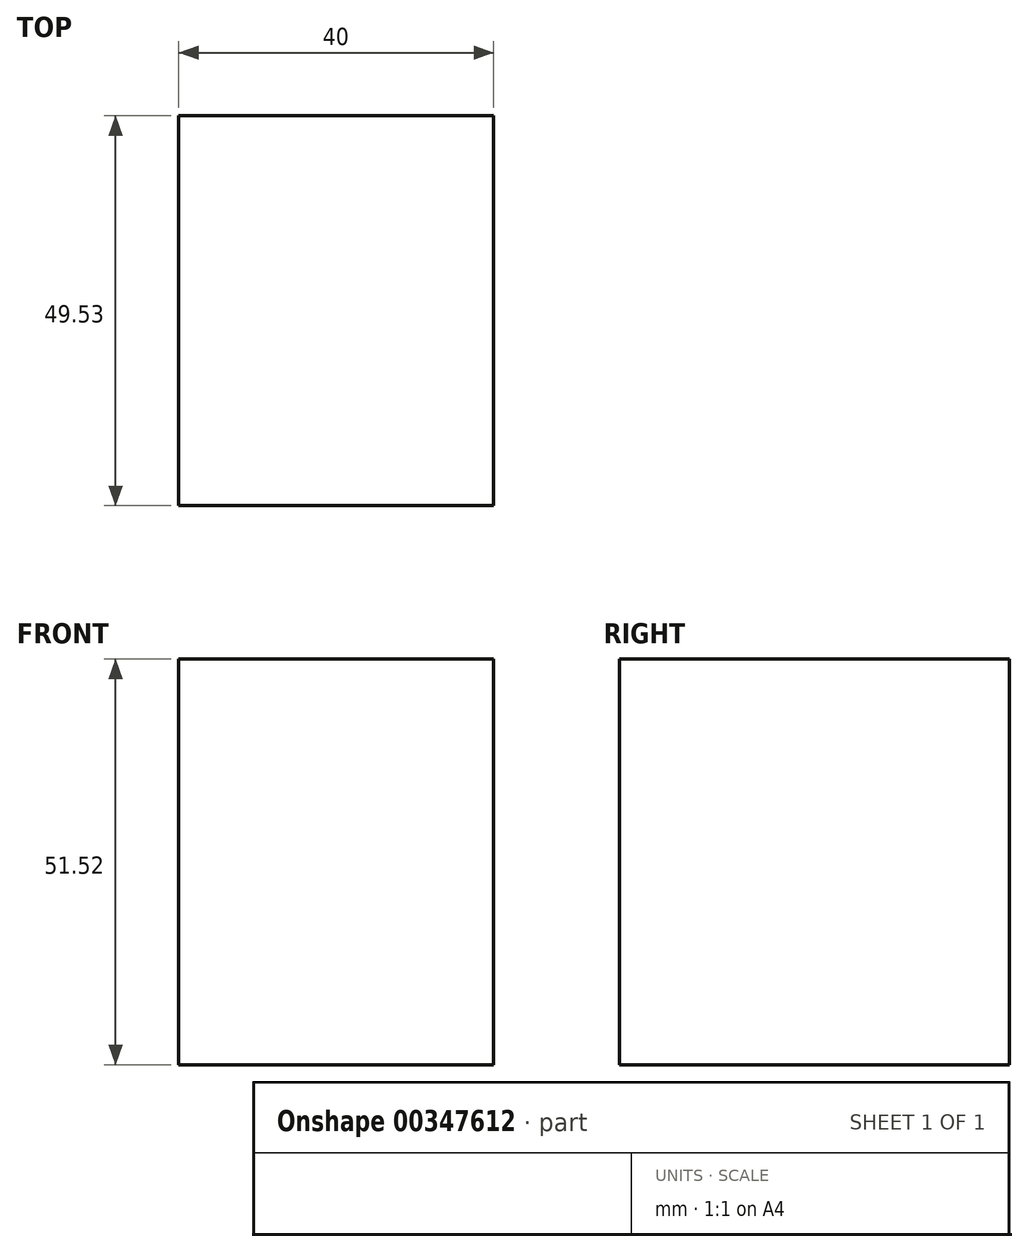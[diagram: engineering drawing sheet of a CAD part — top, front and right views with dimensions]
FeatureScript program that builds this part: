
annotation { "Feature Type Name" : "Feature", "Feature Type Description" : "" }
export const myFeature = defineFeature(function(context is Context, id is Id, definition is map)
    precondition{}
    {
        {
            var Q0;
            Q0=qCreatedBy(makeId("Front.planeOp"),FACE);
            var sketch = newSketch(context, id + "F0", { "sketchPlane" : qUnion([Q0])});
            skLineSegment(sketch, "E0.bottom", {"start": v(-54.68, 26.77) * mm, "end": v(-14.68, 26.77) * mm});
            skLineSegment(sketch, "E0.top", {"start": v(-54.68, -24.75) * mm, "end": v(-14.68, -24.75) * mm});
            skLineSegment(sketch, "E0.left", {"start": v(-54.68, 26.77) * mm, "end": v(-54.68, -24.75) * mm});
            skLineSegment(sketch, "E0.right", {"start": v(-14.68, 26.77) * mm, "end": v(-14.68, -24.75) * mm});
            skSolve(sketch);
        }
        {
            var Q0;
            Q0=makeQuery(id+"F0.imprint","IMPRINT",FACE,{"disambiguationData":[TD([[makeQuery(id+"F0.imprint","IMPRINT",EDGE,{"derivedFrom":sQuery(id+"F0.wireOp",EDGE,"E0.bottom")}),-1.0]])]});
            extrude(context, id + "F1", {"entities" : qUnion([Q0]), "depth" : 49.53 * mm});
        }
    });
